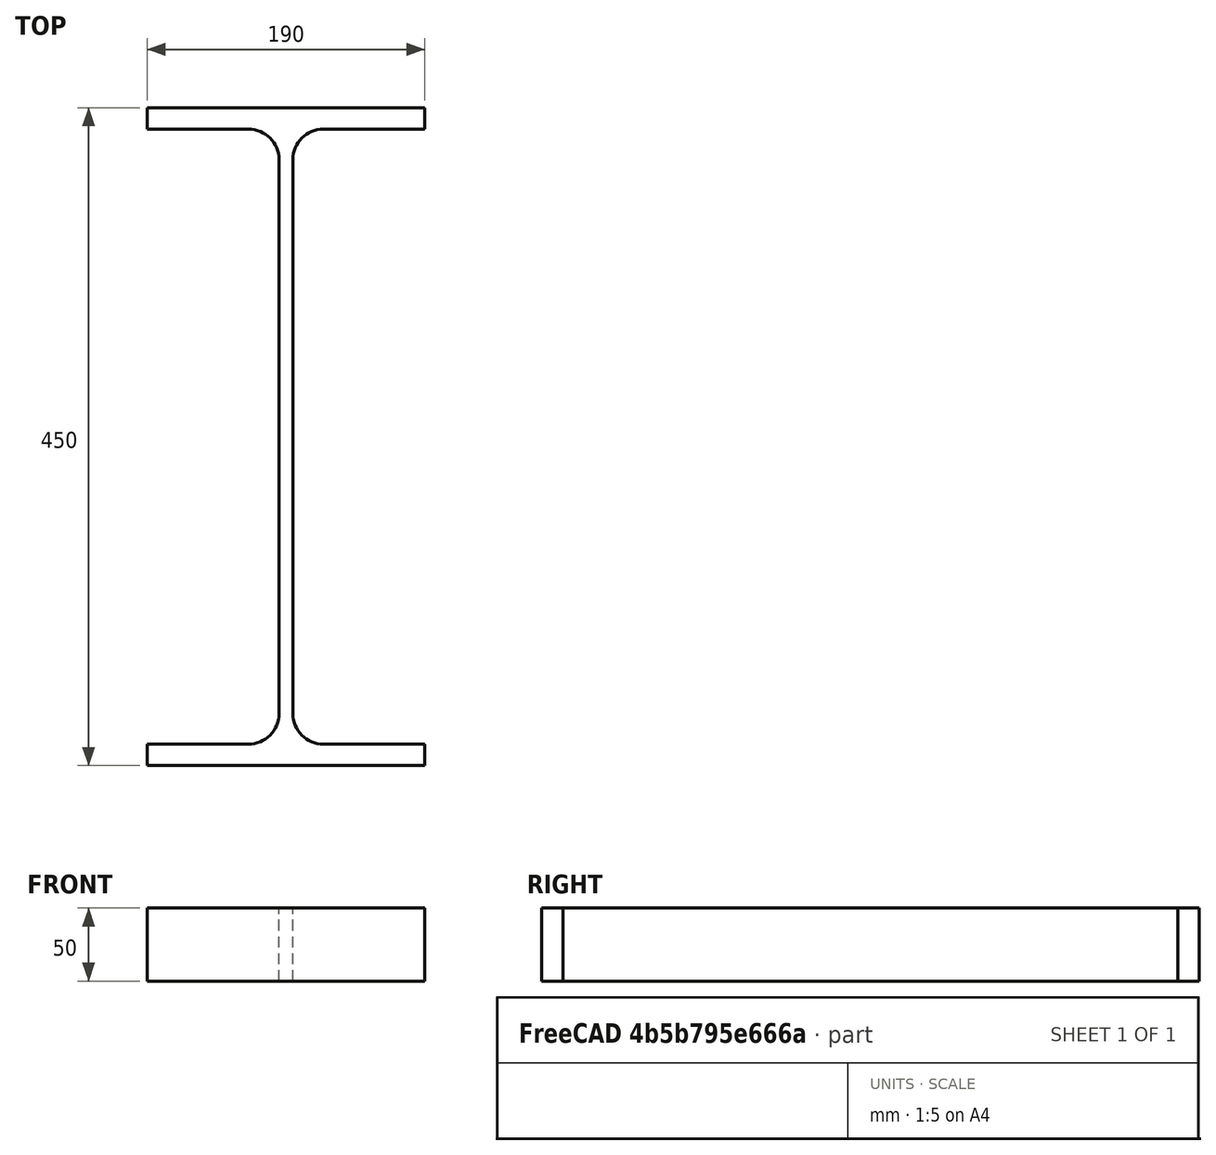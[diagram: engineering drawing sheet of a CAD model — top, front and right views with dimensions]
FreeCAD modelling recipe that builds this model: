
FCSTD DOCUMENT  (FreeCAD 0.15R4671 (Git))
Label: IPE-Profile 450 DIN1025-5 S235JR
License: All rights reserved
LicenseURL: http://en.wikipedia.org/wiki/All_rights_reserved
objects: Sketcher::SketchObject×1, Part::Extrusion×1
note: 2 computed .brp shape members not serialized (recipe doc carries the construction recipe); baked Part::Feature solids carry a one-line shape summary decoded from their .brp

FEATURE [Sketcher::SketchObject] Sketch
  sketch-geometry (16):
    g0: LineSegment StartX=4.7 StartY=-189.4 StartZ=0 EndX=4.7 EndY=189.4 EndZ=0
    g1: LineSegment StartX=25.7 StartY=210.4 StartZ=0 EndX=95 EndY=210.4 EndZ=0
    g2: LineSegment StartX=95 StartY=210.4 StartZ=0 EndX=95 EndY=225 EndZ=0
    g3: LineSegment StartX=95 StartY=225 StartZ=0 EndX=-95 EndY=225 EndZ=0
    g4: LineSegment StartX=-95 StartY=225 StartZ=0 EndX=-95 EndY=210.4 EndZ=0
    g5: LineSegment StartX=-95 StartY=210.4 StartZ=0 EndX=-25.7 EndY=210.4 EndZ=0
    g6: LineSegment StartX=-4.7 StartY=189.4 StartZ=0 EndX=-4.7 EndY=-189.4 EndZ=0
    g7: LineSegment StartX=-25.7 StartY=-210.4 StartZ=0 EndX=-95 EndY=-210.4 EndZ=0
    g8: LineSegment StartX=-95 StartY=-210.4 StartZ=0 EndX=-95 EndY=-225 EndZ=0
    g9: LineSegment StartX=-95 StartY=-225 StartZ=0 EndX=95 EndY=-225 EndZ=0
    g10: LineSegment StartX=95 StartY=-225 StartZ=0 EndX=95 EndY=-210.4 EndZ=0
    g11: LineSegment StartX=95 StartY=-210.4 StartZ=0 EndX=25.7 EndY=-210.4 EndZ=0
    g12: ArcOfCircle CenterX=25.7 CenterY=189.4 CenterZ=0 NormalX=0 NormalY=0 NormalZ=1 Radius=21 StartAngle=1.5708 EndAngle=3.14159
    g13: ArcOfCircle CenterX=25.7 CenterY=-189.4 CenterZ=0 NormalX=0 NormalY=0 NormalZ=1 Radius=21 StartAngle=3.14159 EndAngle=4.71239
    g14: ArcOfCircle CenterX=-25.7 CenterY=189.4 CenterZ=0 NormalX=0 NormalY=0 NormalZ=1 Radius=21 StartAngle=0 EndAngle=1.5708
    g15: ArcOfCircle CenterX=-25.7 CenterY=-189.4 CenterZ=0 NormalX=0 NormalY=0 NormalZ=1 Radius=21 StartAngle=4.71239 EndAngle=6.28319
  constraints (42):
    c: Vertical(g0)
    c: Coincident(g2,g1)
    c: Vertical(g2)
    c: Coincident(g3,g2)
    c: Coincident(g4,g3)
    c: Vertical(g4)
    c: Coincident(g5,g4)
    c: Horizontal(g5)
    c: Vertical(g6)
    c: Horizontal(g7)
    c: Coincident(g8,g7)
    c: Vertical(g8)
    c: Coincident(g9,g8)
    c: Horizontal(g9)
    c: Coincident(g10,g9)
    c: Vertical(g10)
    c: Coincident(g11,g10)
    c: Horizontal(g11)
    c: Tangent(g1,g12) = 1.5708
    c: Tangent(g0,g12) = 1.5708
    c: Tangent(g0,g13) = 1.5708
    c: Tangent(g11,g13) = 1.5708
    c: Tangent(g5,g14) = 1.5708
    c: Tangent(g6,g14) = 1.5708
    c: Tangent(g6,g15) = 1.5708
    c: Tangent(g7,g15) = 1.5708
    c: Equal(g3,g9)
    c: Equal(g2,g4)
    c: Equal(g4,g8)
    c: Equal(g8,g10)
    c: Equal(g12,g14)
    c: Equal(g14,g15)
    c: Equal(g15,g13)
    c: Symmetric(g2,g3,g-2)
    c: Symmetric(g9,g8,g-2)
    c: Symmetric(g0,g6,g-2)
    c: Symmetric(g2,g9,g-1)
    c: DistanceY(g2,g9) = -450
    c: DistanceX(g3) = -190
    c: DistanceX(g0,g6) = -9.4
    c: DistanceY(g2) = 14.6
    c: Radius(g12) = 21
FEATURE [Part::Extrusion] Extrude  label="IPE-Profile 450 DIN1025-5 S235JR"
  Base = -> Sketch
  Dir = (0,0,50)
  Solid = true
